# Revit family: QC-MS-2WAY-CORNER
name_source: partatom
category: Generic Models
revit_build: Autodesk Revit 2018 (Build: 20170223_1515(x64)
units: mm (PartAtom-declared; Revit-internal decimal feet)

## family parameters
Always vertical = Yes
Can host rebar = No
Cut with Voids When Loaded = No
Part Type = Normal
Room Calculation Point = No
Round Connector Dimension = Use Diameter
Shared = No
Work Plane-Based = No

## types (10) — shared parameters
BLADE4WDOWN = QC-BLADE
BLADE4WLEFT = QC-BLADE
BLADE4WR = QC-BLADE
BLADE4WUP = QC-BLADE
Description = STEEL MODULAR CORE DIFFUSER W/ LATTICE FACE PLATE
F1 = 0' - 1"
F10 = 0' - 0 13/32"
F11 = 0' - 0 9/32"
F12 = 0' - 0 1/8"
F2 = 0' - 1 1/16"
F3 = 0' - 0 3/4"
F4 = 0' - 1 15/32"
F5 = 0' - 0 17/32"
F6 = 0' - 0 3/16"
F7 = 0' - 0 1/8"
F8 = 0' - 0 3/16"
F9 = 35.20°
FACEPLATE = 0' - 1 7/8"
FRAMEGAP = 0' - 0 1/8"
Manufacturer = ANEMOSTAT PRODUCTS
Model = QC-MS
Thickness = 0' - 0 1/16"

## per-type parameters (varying)
| type | BLADE4WAY | BLADES | NOMINAL DUCT HI | NOMINAL DUCT WID |
| QC-MS-06X06-2WAY CORNER | 0' - 2 25/32" | 2 | 0' - 6" | 0' - 6" |
| QC-MS-08X08-2WAY CORNER | 0' - 3 23/32" | 2 | 0' - 8" | 0' - 8" |
| QC-MS-10X10-2WAY CORNER | 0' - 4 21/32" | 3 | 0' - 10" | 0' - 10" |
| QC-MS-12X12-2WAY CORNER | 0' - 5 19/32" | 4 | 1' - 0" | 1' - 0" |
| QC-MS-14X14-2WAY CORNER | 0' - 6 1/2" | 4 | 1' - 2" | 1' - 2" |
| QC-MS-16X16-2WAY CORNER | 0' - 7 7/16" | 5 | 1' - 4" | 1' - 4" |
| QC-MS-18X18-2WAY CORNER | 0' - 8 3/8" | 6 | 1' - 6" | 1' - 6" |
| QC-MS-20X20-2WAY CORNER | 0' - 9 5/16" | 6 | 1' - 8" | 1' - 8" |
| QC-MS-22X22-2WAY CORNER | 0' - 10 7/32" | 7 | 1' - 10" | 1' - 10" |
| QC-MS-24X24-2WAY CORNER | 0' - 11 5/32" | 8 | 2' - 0" | 2' - 0" |

## geometry (parser evidence)
native form markers: Sweep x3
no freeform markers — native parametric forms only
